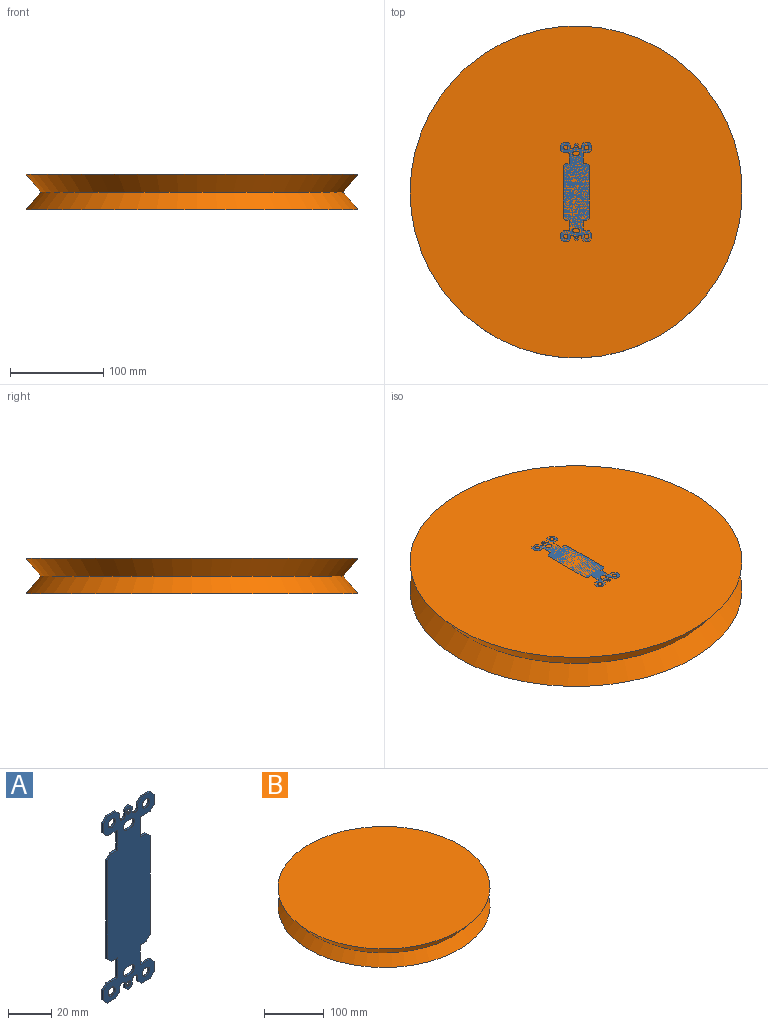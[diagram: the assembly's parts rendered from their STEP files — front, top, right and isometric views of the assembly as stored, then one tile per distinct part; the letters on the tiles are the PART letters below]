
ASSEMBLY  parts=2 mates=1
PART A: 84 faces, bbox 33x1x105.4 mm
  f0: plane 3.98x1.02mm, normal (0,0,1), area 4mm2, adj f1,f67,f68,f69
  f1: plane 10.54x1.02mm, normal (1,0,0), area 10.7mm2, adj f0,f2,f68,f69
  f2: cylinder r=0.76mm len=1.02mm, axis (0,1,0), area 1.2mm2, adj f1,f3,f68,f69
  f3: plane 5.76x1.02mm, normal (0,0,-1), area 5.9mm2, adj f2,f4,f68,f69
  f4: plane 2.54x2.54mm, normal (0.71,0,-0.71), area 3.6mm2, adj f3,f5,f68,f69
  f5: plane 5.84x1.02mm, normal (1,0,0), area 5.9mm2, adj f4,f6,f68,f69
  f6: plane 2.54x2.54mm, normal (0.71,0,0.71), area 3.6mm2, adj f5,f7,f68,f69
  f7: plane 5.61x1.02mm, normal (0,0,1), area 5.7mm2, adj f6,f8,f68,f69
  f8: plane 2.54x2.54mm, normal (-0.71,0,0.71), area 3.6mm2, adj f7,f9,f68,f69
  f9: plane 2.54x1.02mm, normal (-1,0,0), area 2.6mm2, adj f8,f10,f68,f69
  f10: cylinder r=1.52mm len=1.52mm, axis (0,1,0), area 2.4mm2, adj f9,f11,f68,f69
  f11: plane 1.02x0.47mm, normal (0,0,1), area 0.5mm2, adj f10,f12,f68,f69
  f12: cylinder r=1.52mm len=1.52mm, axis (0,1,0), area 2.4mm2, adj f11,f13,f68,f69
  f13: plane 2.79x1.02mm, normal (1,0,0), area 2.8mm2, adj f12,f14,f68,f69
  f14: plane 1.27x1.27mm, normal (0.71,0,0.71), area 1.8mm2, adj f13,f15,f68,f69
  f15: plane 2.06x1.02mm, normal (0,0,1), area 2.1mm2, adj f14,f16,f68,f69
  f16: plane 1.27x1.27mm, normal (-0.71,0,0.71), area 1.8mm2, adj f15,f17,f68,f69
  f17: plane 2.79x1.02mm, normal (-1,0,0), area 2.8mm2, adj f16,f18,f68,f69
  f18: cylinder r=1.52mm len=1.52mm, axis (0,1,0), area 2.4mm2, adj f17,f19,f68,f69
  f19: plane 1.02x0.47mm, normal (0,0,1), area 0.5mm2, adj f18,f20,f68,f69
  f20: cylinder r=1.52mm len=1.52mm, axis (0,1,0), area 2.4mm2, adj f19,f21,f68,f69
  f21: plane 2.54x1.02mm, normal (1,0,0), area 2.6mm2, adj f20,f22,f68,f69
  f22: plane 2.54x2.54mm, normal (0.71,0,0.71), area 3.6mm2, adj f21,f23,f68,f69
  f23: plane 5.61x1.02mm, normal (0,0,1), area 5.7mm2, adj f22,f24,f68,f69
  f24: plane 2.54x2.54mm, normal (-0.71,0,0.71), area 3.6mm2, adj f23,f25,f68,f69
  f25: plane 5.84x1.02mm, normal (-1,0,0), area 5.9mm2, adj f24,f26,f68,f69
  f26: plane 2.54x2.54mm, normal (-0.71,0,-0.71), area 3.6mm2, adj f25,f27,f68,f69
  f27: plane 5.76x1.02mm, normal (0,0,-1), area 5.9mm2, adj f26,f28,f68,f69
  f28: cylinder r=0.76mm len=1.02mm, axis (0,1,0), area 1.2mm2, adj f27,f29,f68,f69
  f29: plane 10.54x1.02mm, normal (-1,0,0), area 10.7mm2, adj f28,f30,f68,f69
  f30: plane 3.98x1.02mm, normal (0,0,1), area 4mm2, adj f29,f31,f68,f69
  f31: plane 2.54x2.54mm, normal (-0.71,0,0.71), area 3.6mm2, adj f30,f32,f68,f69
  f32: plane 55.88x1.02mm, normal (-1,0,0), area 56.8mm2, adj f31,f33,f68,f69
  f33: plane 2.54x2.54mm, normal (-0.71,0,-0.71), area 3.6mm2, adj f32,f34,f68,f69
  f34: plane 3.98x1.02mm, normal (0,0,-1), area 4mm2, adj f33,f35,f68,f69
  f35: plane 10.54x1.02mm, normal (-1,0,0), area 10.7mm2, adj f34,f36,f68,f69
  f36: cylinder r=0.76mm len=1.02mm, axis (0,1,0), area 1.2mm2, adj f35,f37,f68,f69
  f37: plane 5.76x1.02mm, normal (0,0,1), area 5.9mm2, adj f36,f38,f68,f69
  f38: plane 2.54x2.54mm, normal (-0.71,0,0.71), area 3.6mm2, adj f37,f39,f68,f69
  f39: plane 5.84x1.02mm, normal (-1,0,0), area 5.9mm2, adj f38,f40,f68,f69
  f40: plane 2.54x2.54mm, normal (-0.71,0,-0.71), area 3.6mm2, adj f39,f41,f68,f69
  f41: plane 5.61x1.02mm, normal (0,0,-1), area 5.7mm2, adj f40,f42,f68,f69
  f42: plane 2.54x2.54mm, normal (0.71,0,-0.71), area 3.6mm2, adj f41,f43,f68,f69
  f43: plane 2.54x1.02mm, normal (1,0,0), area 2.6mm2, adj f42,f44,f68,f69
  f44: cylinder r=1.52mm len=1.52mm, axis (0,1,0), area 2.4mm2, adj f43,f45,f68,f69
  f45: plane 1.02x0.47mm, normal (0,0,-1), area 0.5mm2, adj f44,f46,f68,f69
  f46: cylinder r=1.52mm len=1.52mm, axis (0,1,0), area 2.4mm2, adj f45,f47,f68,f69
  f47: plane 2.79x1.02mm, normal (-1,0,0), area 2.8mm2, adj f46,f48,f68,f69
  f48: plane 1.27x1.27mm, normal (-0.71,0,-0.71), area 1.8mm2, adj f47,f49,f68,f69
  f49: plane 2.06x1.02mm, normal (0,0,-1), area 2.1mm2, adj f48,f50,f68,f69
  f50: plane 1.27x1.27mm, normal (0.71,0,-0.71), area 1.8mm2, adj f49,f51,f68,f69
  f51: plane 2.79x1.02mm, normal (1,0,0), area 2.8mm2, adj f50,f52,f68,f69
  f52: cylinder r=1.52mm len=1.52mm, axis (0,1,0), area 2.4mm2, adj f51,f53,f68,f69
  f53: plane 1.02x0.47mm, normal (0,0,-1), area 0.5mm2, adj f52,f54,f68,f69
  f54: cylinder r=1.52mm len=1.52mm, axis (0,1,0), area 2.4mm2, adj f53,f55,f68,f69
  f55: plane 2.54x1.02mm, normal (-1,0,0), area 2.6mm2, adj f54,f56,f68,f69
  f56: plane 2.54x2.54mm, normal (-0.71,0,-0.71), area 3.6mm2, adj f55,f57,f68,f69
  f57: plane 5.61x1.02mm, normal (0,0,-1), area 5.7mm2, adj f56,f58,f68,f69
  f58: plane 2.54x2.54mm, normal (0.71,0,-0.71), area 3.6mm2, adj f57,f59,f68,f69
  f59: plane 5.84x1.02mm, normal (1,0,0), area 5.9mm2, adj f58,f60,f68,f69
  f60: plane 2.54x2.54mm, normal (0.71,0,0.71), area 3.6mm2, adj f59,f61,f68,f69
  f61: plane 5.76x1.02mm, normal (0,0,1), area 5.9mm2, adj f60,f62,f68,f69
  f62: cylinder r=0.76mm len=1.02mm, axis (0,1,0), area 1.2mm2, adj f61,f63,f68,f69
  f63: plane 10.54x1.02mm, normal (1,0,0), area 10.7mm2, adj f62,f64,f68,f69
  f64: plane 3.98x1.02mm, normal (0,0,-1), area 4mm2, adj f63,f65,f68,f69
  f65: plane 2.54x2.54mm, normal (0.71,0,-0.71), area 3.6mm2, adj f64,f66,f68,f69
  f66: plane 55.88x1.02mm, normal (1,0,0), area 56.8mm2, adj f65,f67,f68,f69
  f67: plane 2.54x2.54mm, normal (0.71,0,0.71), area 3.6mm2, adj f0,f66,f68,f69
  f68: plane 105.41x33.02mm, normal (0,-1,0), area 2465.1mm2, adj f0,f1,f2,f3,f4,f5,f6,f7
  f69: plane 105.41x33.02mm, normal (0,1,0), area 2465.1mm2, adj f0,f1,f2,f3,f4,f5,f6,f7
  f70: cylinder r=2.38mm len=4.76mm, axis (0,1,0), area 15.2mm2, adj f68,f69
  f71: cylinder r=1.38mm len=2.76mm, axis (0,1,0), area 8.8mm2, adj f68,f69
  f72: cylinder r=2.38mm len=4.76mm, axis (0,1,0), area 15.2mm2, adj f68,f69
  f73: cylinder r=2.38mm len=4.76mm, axis (0,1,0), area 15.2mm2, adj f68,f69
  f74: cylinder r=1.38mm len=2.76mm, axis (0,1,0), area 8.8mm2, adj f68,f69
  f75: cylinder r=2.38mm len=4.76mm, axis (0,1,0), area 15.2mm2, adj f68,f69
  f76: cylinder r=2.41mm len=4.83mm, axis (0,1,0), area 7.7mm2, adj f68,f69,f77,f79
  f77: plane 2.44x1.02mm, normal (0,0,1), area 2.5mm2, adj f68,f69,f76,f78
  f78: cylinder r=2.41mm len=4.83mm, axis (0,1,0), area 7.7mm2, adj f68,f69,f77,f79
  f79: plane 2.44x1.02mm, normal (0,0,-1), area 2.5mm2, adj f68,f69,f76,f78
  f80: cylinder r=2.41mm len=4.83mm, axis (0,1,0), area 7.7mm2, adj f68,f69,f81,f83
  f81: plane 2.44x1.02mm, normal (0,0,1), area 2.5mm2, adj f68,f69,f80,f82
  f82: cylinder r=2.41mm len=4.83mm, axis (0,1,0), area 7.7mm2, adj f68,f69,f81,f83
  f83: plane 2.44x1.02mm, normal (0,0,-1), area 2.5mm2, adj f68,f69,f80,f82
PART B: 4 faces, bbox 355.6x355.6x38.1 mm
  f0: cone r=162.02mm half-angle=39.6deg, axis (0,0,-1), area 26410.9mm2, adj f1,f3
  f1: cone r=177.8mm half-angle=39.6deg, axis (0,0,1), area 26410.9mm2, adj f0,f2
  f2: plane 355.6x355.6mm, normal (0,0,1), area 99314.7mm2, adj f1
  f3: plane 355.6x355.6mm, normal (0,0,-1), area 99314.7mm2, adj f0
PLACE A rot(axis=(-1,0,0),90deg) t=(0,0,18.03)mm
PLACE B at identity
MATE slider A.f68 <-> B.f0  axis (0,0,1) through (0,0,19.05)mm
